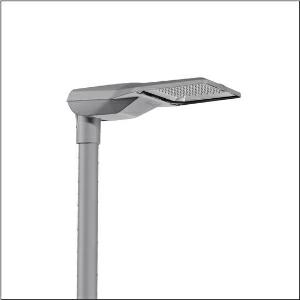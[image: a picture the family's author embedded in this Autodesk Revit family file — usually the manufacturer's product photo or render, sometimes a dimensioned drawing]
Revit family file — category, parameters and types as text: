
# Revit family: streetlight_sl_21_iq_midi___st0_5a_5xe3b41g08nb_d4f3
name_source: partatom
category: Lighting Fixtures
units: mm (PartAtom-declared; Revit-internal decimal feet)

## family parameters
Cut with Voids When Loaded = No
Host = Face
Light Source = No
Part Type = Normal
Room Calculation Point = No
Round Connector Dimension = Use Diameter
Shared = No

## types (1)
- --- (1 x LED, 24250 lm, 155.5 W, 4000K)
    Apparent Load = 155 VA
    CIE Flux Codes = 43 76 97 100 100
    Color Rendering = 70
    Color Temperature = 4000K
    Default Elevation = 1800 mm
    Description = Streetlight SL 21 iQ midi, mast luminaire, primary light control with lens, of PMMA, primary optical cover: cover, of toughened safety glass, transparent, light distribution: ST0.5a, light emission: direct distribution, primary light characteristic: asymmetric, installation type: post-top, side-entry, LED, High Power LED, rated luminous flux: 24.250lm, luminous efficacy: 156lm/W, light colour: 740, colour temperature: 4000K, control: Street-Remote, Auto-Match, Temp-Guard, Lumen-Switch, Night-Set, Smart-Wire, Light-Fading, Desk-Remote (wireless, voltage-free reading and setting of iQ features in the workshop via application-optimized NFC function/RFID function), optimised constant luminous flux control (CLO 2.0), pre-setting: linear dimming characteristic, mains connection: 230..240V, AC, 50/60Hz, start of lifetime: 156W, end of service life: 162W, reduction: 69W, luminaire housing, of diecast aluminium, powder-coated, Siteco® metallic grey (DB 702S), corrosivity category C5 mid according to DIN EN ISO 12944, please order mast flange separately, inclination adjustable: 0°, 5°, 10°, 15°, sealing non-destructively replaceable, multi-level sealing system, length: 644mm, width: 335mm, height: 110mm, mast flange for spigot size: 42mm (side-entry): 5XC10008XM4, 60/48mm (side-entry/post-top): 5XC10108XM2, 76/60mm (side-entry/post-top): 5XC10108XM1, protection rating (complete): IP66, insulation class (complete): insulation class II (safety insulation), certification: CE, ENEC, ENEC+, VDE, impact resistance: IK09, permissible operating ambient temperature for outdoor applications: -40..+50°C, standard-compliant lighting for roads and squares, packaging unit: 1 piece

Light Distribution: ST0.5a
    Height = 111 mm
    Lamp = 1 x LED
    Lamp Light Flux = 24250 lm
    Lamp Power = 155.5 W
    Lamp count = 1
    Length = 644 mm
    Luminous efficacy = 156 lm/W
    Manufacturer = Siteco
    ModVariant = No
    Model = 5XE3B41G08NB
    Number of Poles = 1
    OnlyDefault = Yes
    Power Factor = 1
    Product Name = Streetlight SL 21 iQ midi | ST0.5a
    Product group = mast luminaire | pylon top
    ProductGroupID = 6100
    Protection Class = Protection class II
    Protection Degree = IP 66
    RLX_Detail_Level = 1
    RLX_Emergency_Light_Flux = 0 lm
    RLX_Emergency_Type = 0
    RLX_Emergency_Type_DB = No
    RlxData = <blob elided: 102405 chars, md5=89f281b9>
    Socket = socket
    Standby Power = 0 W
    System Light Flux = 24250 lm
    System Power = 155 W
    Type Comments = factory setting: luminous flux: 100 % | dim-lin: 254 | 823 mA
    Type Image = l_1004298.jpg
    URL = http://relux.com
    VarID = @adj_142423
    Voltage = 0 V
    Weight = 0.00 kg
    Width = 336 mm

## geometry (parser evidence)
native form markers: Blend x4, Sweep x11
no freeform markers — native parametric forms only
